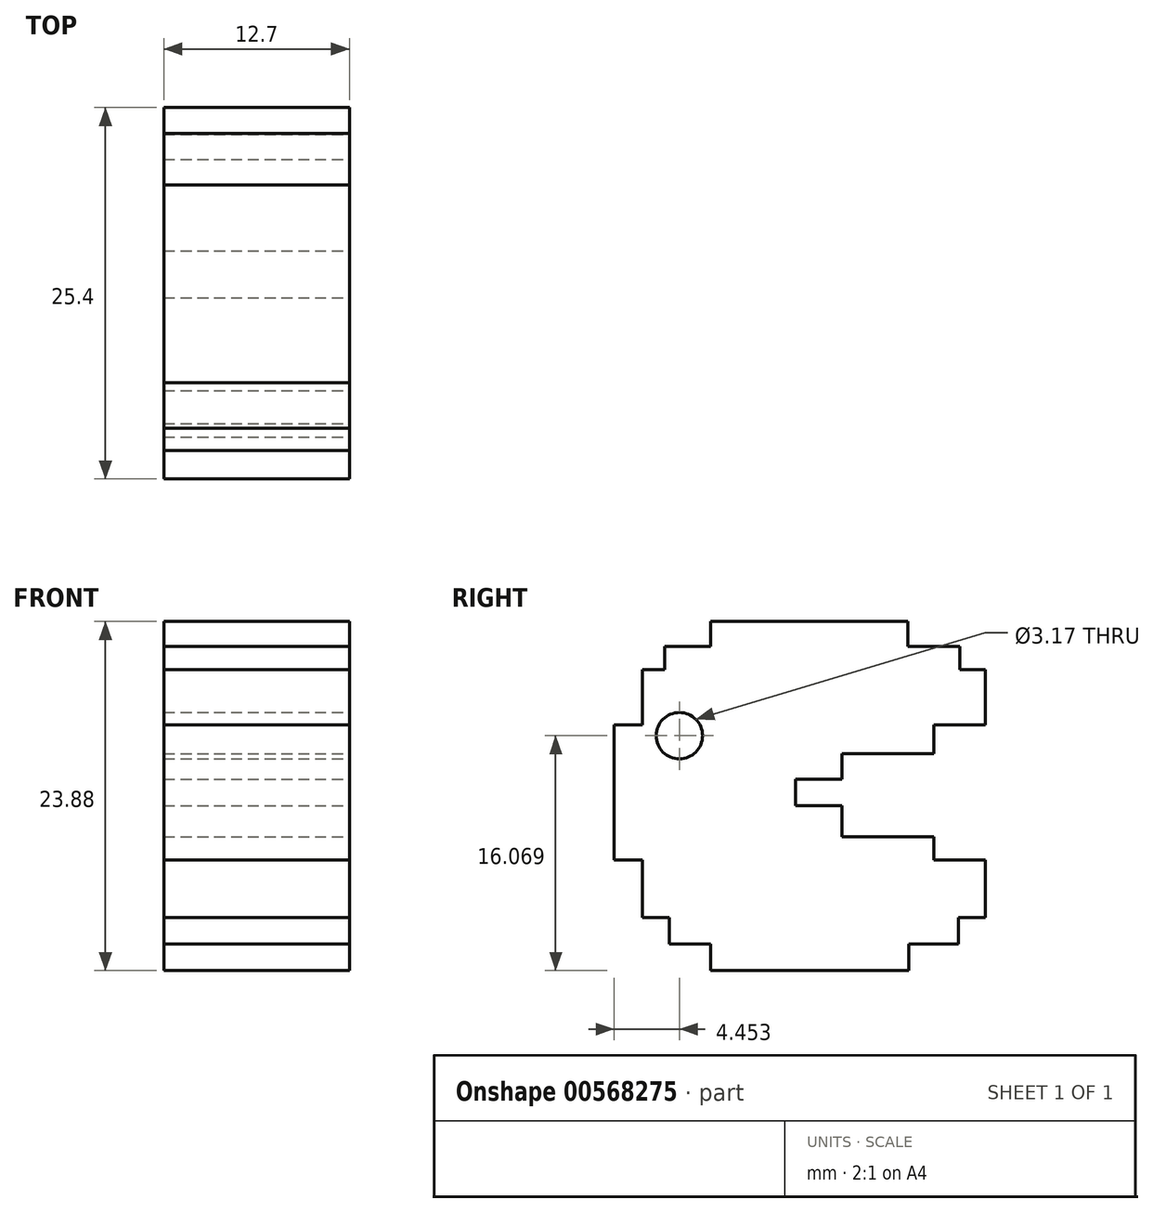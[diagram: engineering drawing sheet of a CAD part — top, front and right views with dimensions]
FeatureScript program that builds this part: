
annotation { "Feature Type Name" : "Feature", "Feature Type Description" : "" }
export const myFeature = defineFeature(function(context is Context, id is Id, definition is map)
    precondition{}
    {
        {
            var Q0;
            Q0=qCreatedBy(makeId("Right.planeOp"),FACE);
            var sketch = newSketch(context, id + "F0", { "sketchPlane" : qUnion([Q0])});
            skLineSegment(sketch, "E0", {"start": v(0, 0) * mm, "end": v(0, 25.4) * mm});
            skLineSegment(sketch, "E1", {"start": v(0, 25.4) * mm, "end": v(25.4, 25.4) * mm});
            skLineSegment(sketch, "E2", {"start": v(25.4, 25.4) * mm, "end": v(25.4, 0) * mm});
            skLineSegment(sketch, "E3", {"start": v(25.4, 0) * mm, "end": v(0, 0) * mm});
            skSolve(sketch);
        }
        {
            var Q0;
            Q0 = qSketchRegion(id + "F0", true);
            extrude(context, id + "F1", {"entities" : qUnion([Q0]), "depth" : 12.7 * mm, "offsetDistance" : 25.4 * mm});
        }
        {
            var Q0;
            Q0=makeQuery(id+"F1.opExtrude","CAP_FACE",FACE,{"disambiguationData":[OSD([sQuery(id+"F0.wireOp",EDGE,"E0"),sQuery(id+"F0.wireOp",EDGE,"E1"),sQuery(id+"F0.wireOp",EDGE,"E2"),sQuery(id+"F0.wireOp",EDGE,"E3")])],"isStart":false});
            var sketch = newSketch(context, id + "F2", { "sketchPlane" : qUnion([Q0])});
            skLineSegment(sketch, "E4", {"start": v(6.59, 0) * mm, "end": v(20.14, 0) * mm});
            skLineSegment(sketch, "E5", {"start": v(20.14, 0) * mm, "end": v(20.14, 1.84) * mm});
            skLineSegment(sketch, "E6", {"start": v(20.14, 1.84) * mm, "end": v(23.56, 1.84) * mm});
            skLineSegment(sketch, "E7", {"start": v(23.56, 1.84) * mm, "end": v(23.56, 3.63) * mm});
            skLineSegment(sketch, "E8", {"start": v(23.56, 3.63) * mm, "end": v(25.4, 3.63) * mm});
            skLineSegment(sketch, "E9", {"start": v(25.4, 3.63) * mm, "end": v(25.4, 7.55) * mm});
            skLineSegment(sketch, "E10", {"start": v(25.4, 7.55) * mm, "end": v(21.85, 7.55) * mm});
            skPoint(sketch, "E10.endSnap0", {"position": v(21.85, 1.84) * mm});
            skLineSegment(sketch, "E11", {"start": v(21.85, 7.55) * mm, "end": v(21.85, 9.17) * mm});
            skLineSegment(sketch, "E12", {"start": v(21.85, 9.17) * mm, "end": v(15.58, 9.17) * mm});
            skLineSegment(sketch, "E13", {"start": v(15.58, 9.17) * mm, "end": v(15.58, 11.29) * mm});
            skLineSegment(sketch, "E14", {"start": v(15.58, 11.29) * mm, "end": v(12.4, 11.29) * mm});
            skLineSegment(sketch, "E15", {"start": v(12.4, 11.29) * mm, "end": v(12.4, 13.09) * mm});
            skLineSegment(sketch, "E16", {"start": v(12.4, 13.09) * mm, "end": v(15.58, 13.09) * mm});
            skLineSegment(sketch, "E17", {"start": v(15.58, 13.09) * mm, "end": v(15.58, 14.84) * mm});
            skLineSegment(sketch, "E18", {"start": v(15.58, 14.84) * mm, "end": v(21.85, 14.84) * mm});
            skLineSegment(sketch, "E19", {"start": v(21.85, 14.84) * mm, "end": v(21.85, 16.82) * mm});
            skLineSegment(sketch, "E20", {"start": v(21.85, 16.82) * mm, "end": v(25.4, 16.82) * mm});
            skLineSegment(sketch, "E21", {"start": v(25.4, 16.82) * mm, "end": v(25.4, 20.6) * mm});
            skLineSegment(sketch, "E22", {"start": v(25.4, 20.6) * mm, "end": v(23.62, 20.6) * mm});
            skPoint(sketch, "E22.endSnap0", {"position": v(23.62, 16.82) * mm});
            skLineSegment(sketch, "E23", {"start": v(23.62, 20.6) * mm, "end": v(23.62, 22.17) * mm});
            skLineSegment(sketch, "E24", {"start": v(23.62, 22.17) * mm, "end": v(20.1, 22.17) * mm});
            skLineSegment(sketch, "E25", {"start": v(20.1, 22.17) * mm, "end": v(20.1, 23.88) * mm});
            skLineSegment(sketch, "E26", {"start": v(20.1, 23.88) * mm, "end": v(6.59, 23.88) * mm});
            skLineSegment(sketch, "E27", {"start": v(6.59, 23.88) * mm, "end": v(6.59, 22.17) * mm});
            skLineSegment(sketch, "E28", {"start": v(6.59, 22.17) * mm, "end": v(3.45, 22.17) * mm});
            skLineSegment(sketch, "E29", {"start": v(3.45, 22.17) * mm, "end": v(3.45, 20.6) * mm});
            skLineSegment(sketch, "E30", {"start": v(3.45, 20.6) * mm, "end": v(1.93, 20.6) * mm});
            skLineSegment(sketch, "E31", {"start": v(1.93, 20.6) * mm, "end": v(1.93, 16.82) * mm});
            skLineSegment(sketch, "E32", {"start": v(1.93, 16.82) * mm, "end": v(0, 16.82) * mm});
            skLineSegment(sketch, "E33", {"start": v(0, 16.82) * mm, "end": v(0, 7.55) * mm});
            skLineSegment(sketch, "E34", {"start": v(0, 7.55) * mm, "end": v(1.93, 7.55) * mm});
            skLineSegment(sketch, "E35", {"start": v(1.93, 7.55) * mm, "end": v(1.93, 3.63) * mm});
            skLineSegment(sketch, "E36", {"start": v(1.93, 3.63) * mm, "end": v(3.78, 3.63) * mm});
            skLineSegment(sketch, "E37", {"start": v(3.78, 3.63) * mm, "end": v(3.78, 1.84) * mm});
            skLineSegment(sketch, "E38", {"start": v(3.78, 1.84) * mm, "end": v(6.59, 1.84) * mm});
            skLineSegment(sketch, "E39", {"start": v(6.59, 1.84) * mm, "end": v(6.59, 0) * mm});
            skSolve(sketch);
        }
        {
            var Q0;
            {var subQ0=sQuery(id+"F2.wireOp",EDGE,"E22");Q0=makeQuery(id+"F2.imprint","IMPRINT",FACE,{"disambiguationData":[TD([[makeQuery(id+"F2.imprint","IMPRINT",EDGE,{"derivedFrom":subQ0}),-1.0]])]});}
            var Q1;
            {var subQ4=sQuery(id+"F2.wireOp",EDGE,"E34");Q1=makeQuery(id+"F2.imprint","IMPRINT",FACE,{"disambiguationData":[TD([[makeQuery(id+"F2.imprint","IMPRINT",EDGE,{"derivedFrom":subQ4}),-1.0]])]});}
            var Q2;
            {var subQ1=sQuery(id+"F2.wireOp",EDGE,"E5");Q2=makeQuery(id+"F2.imprint","IMPRINT",FACE,{"disambiguationData":[TD([[makeQuery(id+"F2.imprint","IMPRINT",EDGE,{"derivedFrom":subQ1}),-1.0]])]});}
            var Q3;
            {var subQ0=sQuery(id+"F2.wireOp",EDGE,"E10");Q3=makeQuery(id+"F2.imprint","IMPRINT",FACE,{"disambiguationData":[TD([[makeQuery(id+"F2.imprint","IMPRINT",EDGE,{"derivedFrom":subQ0}),-1.0]])]});}
            extrude(context, id + "F3", {"entities" : qUnion([Q0, Q1, Q2, Q3]), "operationType" : NewBodyOperationType.REMOVE, "oppositeDirection" : true, "depth" : 25.4 * mm, "offsetDistance" : 25.4 * mm});
        }
        {
            var Q0;
            Q0=makeQuery(id+"F1.opExtrude","CAP_FACE",FACE,{"disambiguationData":[OSD([sQuery(id+"F0.wireOp",EDGE,"E0"),sQuery(id+"F0.wireOp",EDGE,"E1"),sQuery(id+"F0.wireOp",EDGE,"E2"),sQuery(id+"F0.wireOp",EDGE,"E3")])],"isStart":false});
            var sketch = newSketch(context, id + "F4", { "sketchPlane" : qUnion([Q0])});
            skCircle(sketch, "E40", {"center": v(4.45, 16.07) * mm, "radius": 1.59 * mm});
            skSolve(sketch);
        }
        {
            var Q0;
            Q0 = qSketchRegion(id + "F4", true);
            extrude(context, id + "F5", {"entities" : qUnion([Q0]), "operationType" : NewBodyOperationType.REMOVE, "oppositeDirection" : true, "depth" : 12.7 * mm, "offsetDistance" : 25.4 * mm});
        }
    });
